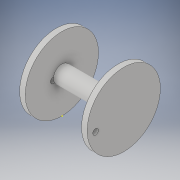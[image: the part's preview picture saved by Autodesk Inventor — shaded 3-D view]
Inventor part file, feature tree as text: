
AUTODESK INVENTOR PART (.ipt)
format: ipt  version: 2019 (Build 230136000, 136)  size: 122,368 bytes
history: native  units: in
note: dims shown in document units (in); Inventor stores cm internally (conversion verified against a paired STEP export)
features: sketch x5, hole x2, revolve x1
ambient origin geometry x8: Origin, YZ Plane, XZ Plane, XY Plane, X Axis, Y Axis, Z Axis, Center Point
bodies: Solid1 (feature_tree)
feature tree (8):
  revolve  "Revolution1"  [1 undecoded]
  hole  "Hole1"  [1 undecoded]
  hole  "Hole2"  [1 undecoded]
  sketch  "Sketch4"  dims[d6=0.0787in d7=0.2362in d8=0.1575in d9=0.0787in d10=90.0deg d11=0.315in d12=0.8108in]
  sketch  "Sketch5"  dims[d13=0.0787in d14=0.2362in d15=0.1575in d16=0.0787in d17=90.0deg d18=0.315in d19=0.8108in]
  sketch  "Sketch1"  dims[d0=0.5118in d1=0.9449in]
  sketch  "Sketch2"  dims[d2=0.0787in d3=0.3937in]
  sketch  "Sketch3"  dims[d4=0.7874in d5=90.0deg]
note: 3 required parameter values undecoded (feature->parameter linkage not recoverable at this tier; creation-order binding heuristic only, values carry confidence <= 0.55)